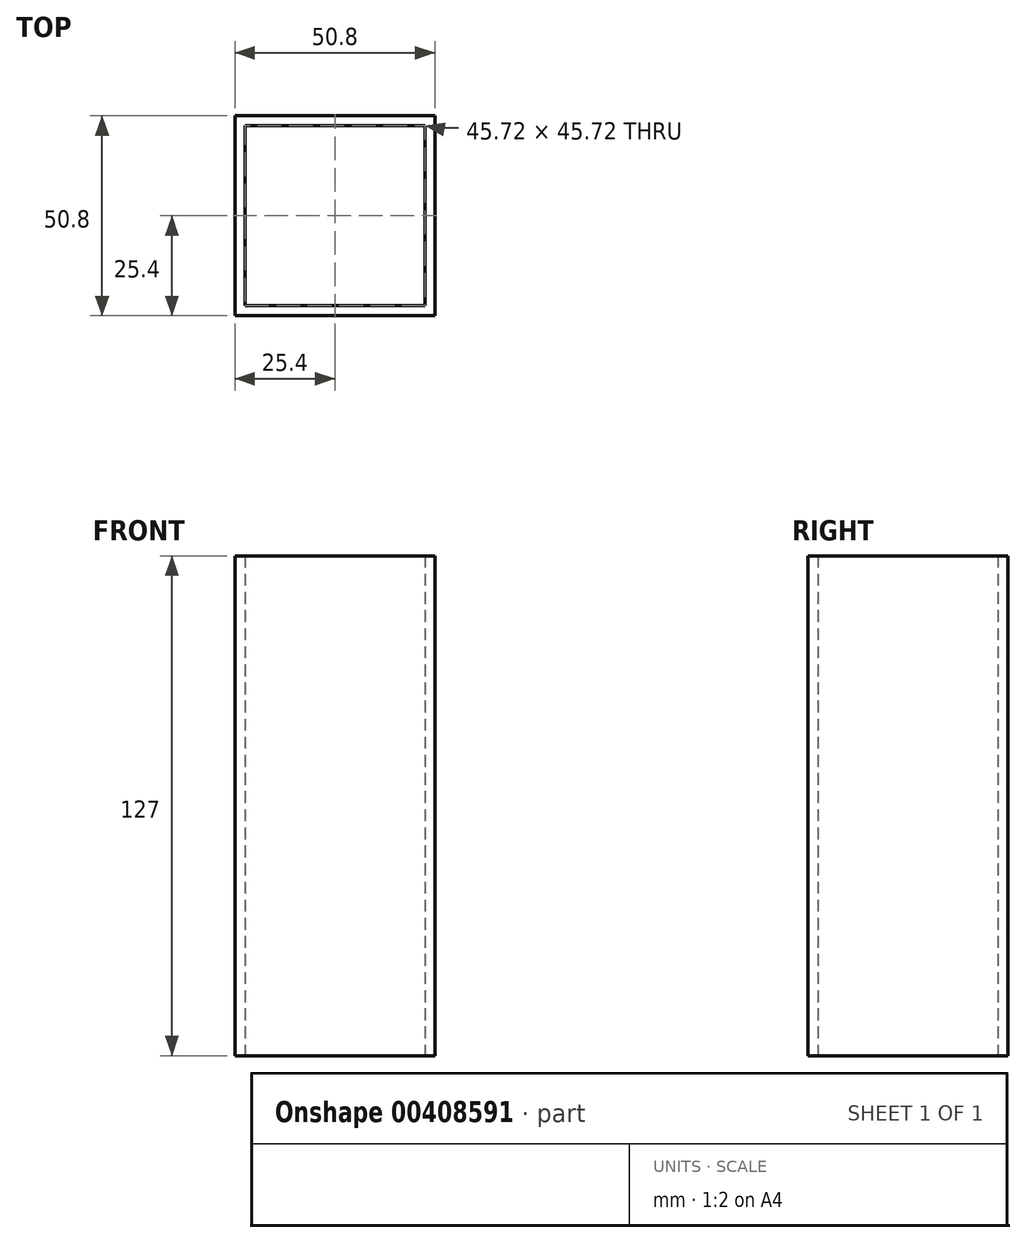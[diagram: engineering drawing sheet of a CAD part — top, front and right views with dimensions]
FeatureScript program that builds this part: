
annotation { "Feature Type Name" : "Feature", "Feature Type Description" : "" }
export const myFeature = defineFeature(function(context is Context, id is Id, definition is map)
    precondition{}
    {
        {
            var Q0;
            Q0=qCreatedBy(makeId("Top.planeOp"),FACE);
            var sketch = newSketch(context, id + "F0", { "sketchPlane" : qUnion([Q0])});
            skLineSegment(sketch, "E0.bottom", {"start": v(25.4, -25.4) * mm, "end": v(-25.4, -25.4) * mm});
            skLineSegment(sketch, "E0.top", {"start": v(25.4, 25.4) * mm, "end": v(-25.4, 25.4) * mm});
            skLineSegment(sketch, "E0.left", {"start": v(25.4, -25.4) * mm, "end": v(25.4, 25.4) * mm});
            skLineSegment(sketch, "E0.right", {"start": v(-25.4, -25.4) * mm, "end": v(-25.4, 25.4) * mm});
            skPoint(sketch, "E0.middle", {"position": v(0, 0) * mm});
            skSolve(sketch);
        }
        {
            var Q0;
            Q0=makeQuery(id+"F0.imprint","IMPRINT",FACE,{"disambiguationData":[TD([[makeQuery(id+"F0.imprint","IMPRINT",EDGE,{"derivedFrom":sQuery(id+"F0.wireOp",EDGE,"E0.bottom")}),-1.0]])]});
            extrude(context, id + "F1", {"entities" : qUnion([Q0]), "endBound" : BoundingType.SYMMETRIC, "depth" : 127 * mm});
        }
        {
            var Q0;
            Q0=makeQuery(id+"F1.opExtrude","CAP_FACE",FACE,{"disambiguationData":[OSD([sQuery(id+"F0.wireOp",EDGE,"E0.bottom"),sQuery(id+"F0.wireOp",EDGE,"E0.top"),sQuery(id+"F0.wireOp",EDGE,"E0.left"),sQuery(id+"F0.wireOp",EDGE,"E0.right")])],"isStart":false});
            var Q1;
            Q1=makeQuery(id+"F1.opExtrude","CAP_FACE",FACE,{"disambiguationData":[OSD([sQuery(id+"F0.wireOp",EDGE,"E0.bottom"),sQuery(id+"F0.wireOp",EDGE,"E0.top"),sQuery(id+"F0.wireOp",EDGE,"E0.left"),sQuery(id+"F0.wireOp",EDGE,"E0.right")])],"isStart":true});
            shell(context, id + "F2", {"entities" : qUnion([Q0, Q1]), "thickness" : 2.54 * mm});
        }
    });
